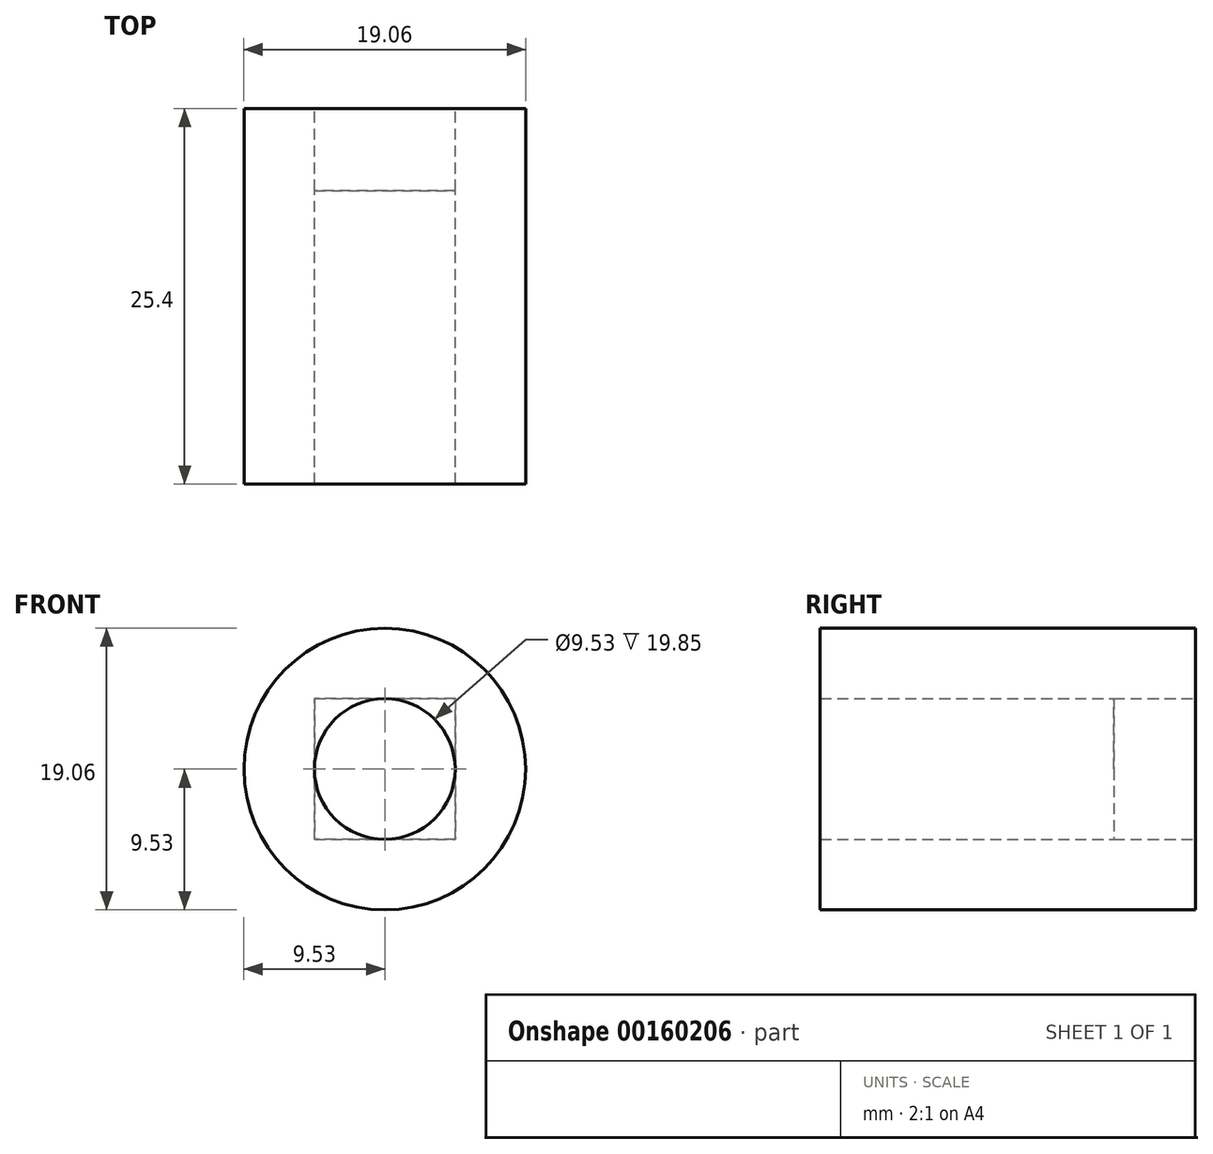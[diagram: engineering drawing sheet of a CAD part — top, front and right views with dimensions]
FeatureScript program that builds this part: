
annotation { "Feature Type Name" : "Feature", "Feature Type Description" : "" }
export const myFeature = defineFeature(function(context is Context, id is Id, definition is map)
    precondition{}
    {
        {
            var Q0;
            Q0=qCreatedBy(makeId("Front.planeOp"),FACE);
            var sketch = newSketch(context, id + "F0", { "sketchPlane" : qUnion([Q0])});
            skCircle(sketch, "E0", {"center": v(0, 0) * mm, "radius": 9.53 * mm});
            skSolve(sketch);
        }
        {
            var Q0;
            Q0 = qSketchRegion(id + "F0", true);
            extrude(context, id + "F1", {"entities" : qUnion([Q0]), "depth" : 25.4 * mm});
        }
        {
            var Q0;
            Q0=qCreatedBy(makeId("Front.planeOp"),FACE);
            var sketch = newSketch(context, id + "F2", { "sketchPlane" : qUnion([Q0])});
            skLineSegment(sketch, "E1.bottom", {"start": v(-4.76, 4.76) * mm, "end": v(4.76, 4.76) * mm});
            skLineSegment(sketch, "E1.top", {"start": v(-4.76, -4.76) * mm, "end": v(4.76, -4.76) * mm});
            skLineSegment(sketch, "E1.left", {"start": v(-4.76, 4.76) * mm, "end": v(-4.76, -4.76) * mm});
            skLineSegment(sketch, "E1.right", {"start": v(4.76, 4.76) * mm, "end": v(4.76, -4.76) * mm});
            skPoint(sketch, "E1.middle", {"position": v(0, 0) * mm});
            skCircle(sketch, "E2", {"center": v(0, 0) * mm, "radius": 4.76 * mm});
            skSolve(sketch);
        }
        {
            var Q0;
            {var subQ0=sQuery(id+"F2.wireOp",EDGE,"E2");var subQ1=makeQuery(id+"F2.imprint","INTERSECT",VERTEX,{"derivedFrom":[sQuery(id+"F2.wireOp",EDGE,"E1.bottom"),subQ0]});Q0=makeQuery(id+"F2.imprint","IMPRINT",FACE,{"disambiguationData":[TD([[makeQuery(id+"F2.imprint","IMPRINT",EDGE,{"disambiguationData":[TD([[subQ1,1.0]])],"derivedFrom":subQ0}),1.0]])]});}
            extrude(context, id + "F3", {"entities" : qUnion([Q0]), "operationType" : NewBodyOperationType.REMOVE, "endBound" : BoundingType.THROUGH_ALL, "depth" : 25.4 * mm});
        }
        {
            var Q0;
            Q0 = qSketchRegion(id + "F2", true);
            extrude(context, id + "F4", {"entities" : qUnion([Q0]), "operationType" : NewBodyOperationType.REMOVE, "endBound" : BoundingType.SYMMETRIC, "depth" : 11.1 * mm});
        }
    });
